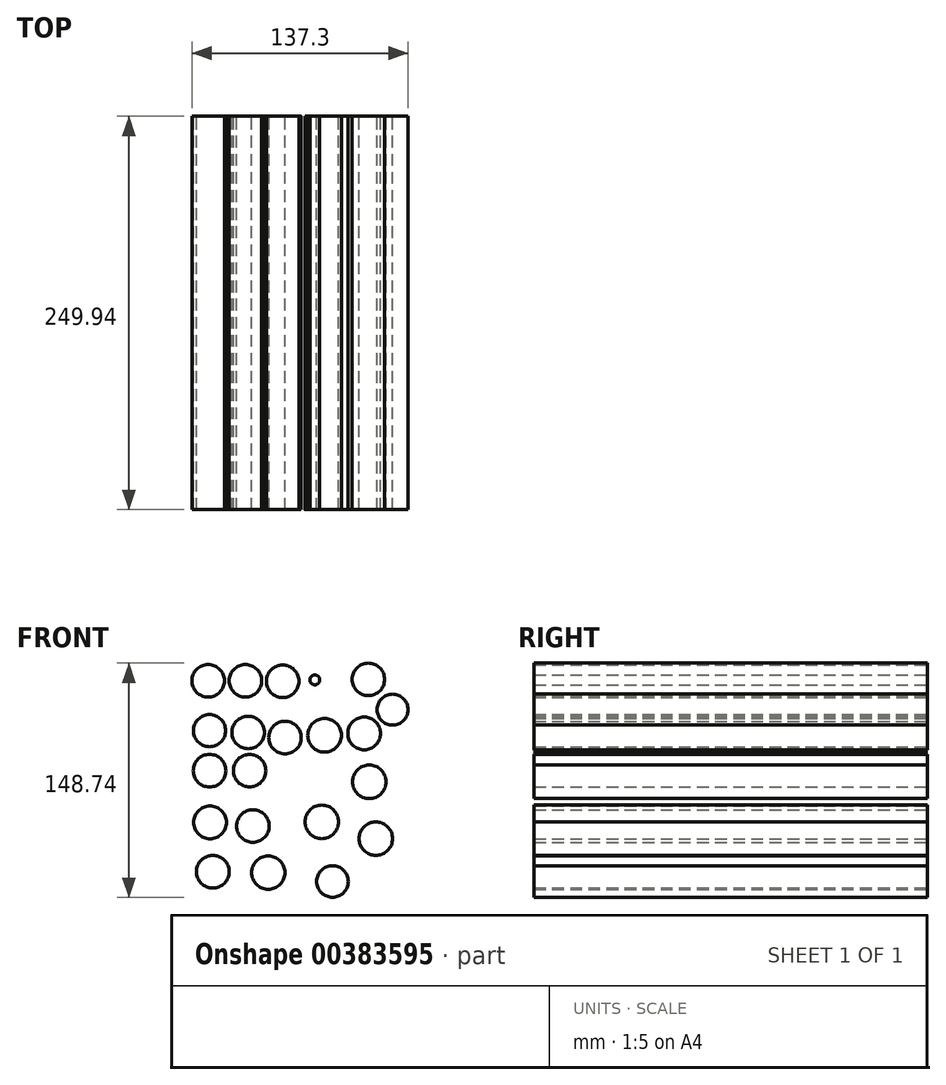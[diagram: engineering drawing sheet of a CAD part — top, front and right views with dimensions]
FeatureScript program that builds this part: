
annotation { "Feature Type Name" : "Feature", "Feature Type Description" : "" }
export const myFeature = defineFeature(function(context is Context, id is Id, definition is map)
    precondition{}
    {
        {
            var Q0;
            Q0=qCreatedBy(makeId("Front.planeOp"),FACE);
            var sketch = newSketch(context, id + "F0", { "sketchPlane" : qUnion([Q0])});
            skCircle(sketch, "E0", {"center": v(-58.27, 64.19) * mm, "radius": 10.33 * mm});
            skCircle(sketch, "E1", {"center": v(-34.6, 64.19) * mm, "radius": 10.33 * mm});
            skCircle(sketch, "E2", {"center": v(-10.94, 63.9) * mm, "radius": 10.35 * mm});
            skCircle(sketch, "E3", {"center": v(9.47, 64.78) * mm, "radius": 3.14 * mm});
            skCircle(sketch, "E4", {"center": v(-57.38, 32.54) * mm, "radius": 10.2 * mm});
            skCircle(sketch, "E5", {"center": v(-32.83, 31.35) * mm, "radius": 10.3 * mm});
            skCircle(sketch, "E6", {"center": v(-9.47, 28.1) * mm, "radius": 10.33 * mm});
            skCircle(sketch, "E7", {"center": v(-57.38, 7.1) * mm, "radius": 10.35 * mm});
            skCircle(sketch, "E8", {"center": v(-31.95, 7.1) * mm, "radius": 10.32 * mm});
            skCircle(sketch, "E9", {"center": v(-57.09, -25.73) * mm, "radius": 10.42 * mm});
            skCircle(sketch, "E10", {"center": v(-29.88, -28.1) * mm, "radius": 10.36 * mm});
            skCircle(sketch, "E11", {"center": v(-55.31, -57.09) * mm, "radius": 10.4 * mm});
            skCircle(sketch, "E12", {"center": v(-20.11, -57.68) * mm, "radius": 10.6 * mm});
            skCircle(sketch, "E13", {"center": v(13.9, -25.44) * mm, "radius": 10.67 * mm});
            skCircle(sketch, "E14", {"center": v(20.7, -63.3) * mm, "radius": 10.06 * mm});
            skCircle(sketch, "E15", {"center": v(40.82, 30.76) * mm, "radius": 10.4 * mm});
            skCircle(sketch, "E16", {"center": v(15.68, 29.58) * mm, "radius": 10.69 * mm});
            skCircle(sketch, "E17", {"center": v(48.21, -36.09) * mm, "radius": 10.67 * mm});
            skCircle(sketch, "E18", {"center": v(43.48, 65.08) * mm, "radius": 10.3 * mm});
            skCircle(sketch, "E19", {"center": v(58.86, 45.85) * mm, "radius": 9.83 * mm});
            skCircle(sketch, "E20", {"center": v(44.07, 0) * mm, "radius": 10.67 * mm});
            skSolve(sketch);
        }
        {
            var Q0;
            Q0 = qSketchRegion(id + "F0", true);
            extrude(context, id + "F1", {"entities" : qUnion([Q0]), "endBound" : BoundingType.SYMMETRIC, "depth" : 249.94 * mm});
        }
    });
